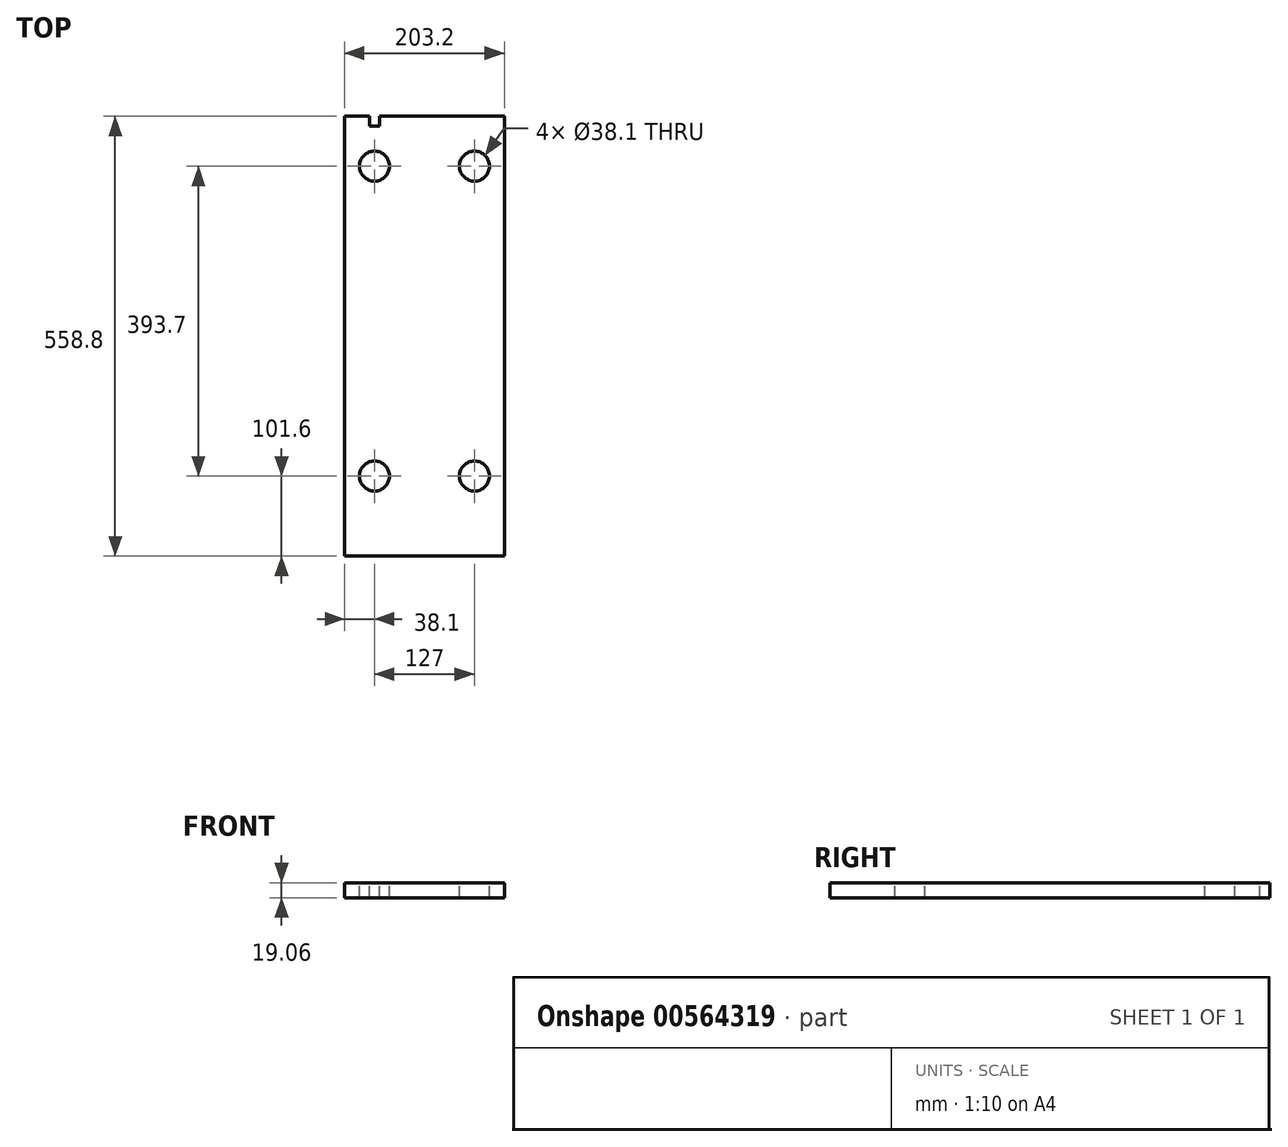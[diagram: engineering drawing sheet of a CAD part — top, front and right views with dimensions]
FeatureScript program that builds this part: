
annotation { "Feature Type Name" : "Feature", "Feature Type Description" : "" }
export const myFeature = defineFeature(function(context is Context, id is Id, definition is map)
    precondition{}
    {
        {
            var Q0;
            Q0=qCreatedBy(makeId("Front.planeOp"),FACE);
            var sketch = newSketch(context, id + "F0", { "sketchPlane" : qUnion([Q0])});
            skLineSegment(sketch, "E0.bottom", {"start": v(-101.6, 9.53) * mm, "end": v(101.6, 9.53) * mm});
            skLineSegment(sketch, "E0.top", {"start": v(-101.6, -9.53) * mm, "end": v(101.6, -9.53) * mm});
            skLineSegment(sketch, "E0.left", {"start": v(-101.6, 9.53) * mm, "end": v(-101.6, -9.53) * mm});
            skLineSegment(sketch, "E0.right", {"start": v(101.6, 9.53) * mm, "end": v(101.6, -9.53) * mm});
            skPoint(sketch, "E0.middle", {"position": v(0, 0) * mm});
            skSolve(sketch);
        }
        {
            var Q0;
            Q0 = qSketchRegion(id + "F0", true);
            extrude(context, id + "F1", {"entities" : qUnion([Q0]), "depth" : 558.8 * mm, "offsetDistance" : 25.4 * mm});
        }
        {
            var Q0;
            Q0=makeQuery(id+"F1.opExtrude","SWEPT_FACE",FACE,{"disambiguationData":[OSD([sQuery(id+"F0.wireOp",EDGE,"E0.bottom")])]});
            var sketch = newSketch(context, id + "F2", { "sketchPlane" : qUnion([Q0])});
            skLineSegment(sketch, "E1", {"start": v(0, 0) * mm, "end": v(0, -627.02) * mm, "construction": true});
            skPoint(sketch, "E1.endSnap0", {"position": v(0, -558.8) * mm});
            skCircle(sketch, "E2", {"center": v(-63.5, -63.5) * mm, "radius": 19.05 * mm});
            skCircle(sketch, "E3", {"center": v(63.5, -63.5) * mm, "radius": 19.05 * mm});
            skCircle(sketch, "E4", {"center": v(-63.5, -457.2) * mm, "radius": 19.05 * mm});
            skCircle(sketch, "E5", {"center": v(63.5, -457.2) * mm, "radius": 19.05 * mm});
            skLineSegment(sketch, "E6.bottom", {"start": v(-69.85, 0) * mm, "end": v(-57.15, 0) * mm});
            skLineSegment(sketch, "E6.top", {"start": v(-69.85, -12.7) * mm, "end": v(-57.15, -12.7) * mm});
            skLineSegment(sketch, "E6.left", {"start": v(-69.85, 0) * mm, "end": v(-69.85, -12.7) * mm});
            skLineSegment(sketch, "E6.right", {"start": v(-57.15, 0) * mm, "end": v(-57.15, -12.7) * mm});
            skSolve(sketch);
        }
        {
            var Q0;
            Q0 = qSketchRegion(id + "F2", true);
            extrude(context, id + "F3", {"entities" : qUnion([Q0]), "operationType" : NewBodyOperationType.REMOVE, "oppositeDirection" : true, "depth" : 25.4 * mm, "offsetDistance" : 25.4 * mm});
        }
    });
